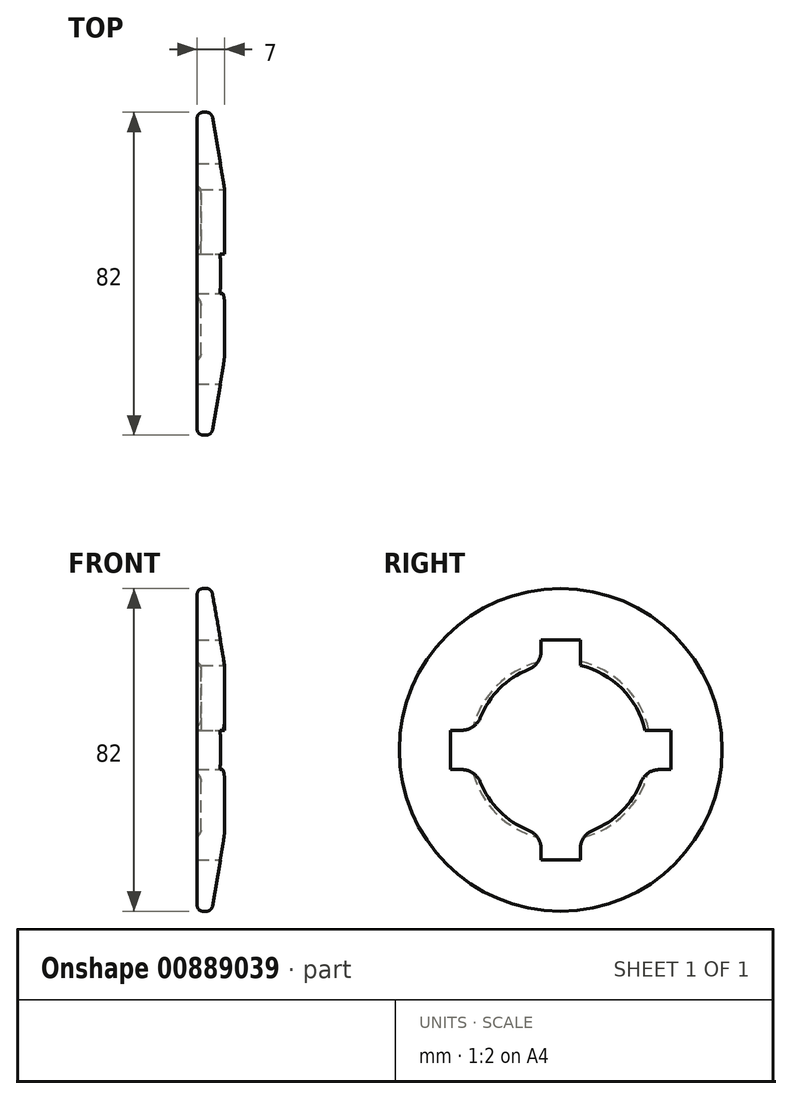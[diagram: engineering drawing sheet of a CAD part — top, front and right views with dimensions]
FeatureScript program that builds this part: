
annotation { "Feature Type Name" : "Feature", "Feature Type Description" : "" }
export const myFeature = defineFeature(function(context is Context, id is Id, definition is map)
    precondition{}
    {
        {
            var Q0;
            Q0=qCreatedBy(makeId("Front.planeOp"),FACE);
            var sketch = newSketch(context, id + "F0", { "sketchPlane" : qUnion([Q0])});
            skLineSegment(sketch, "E0", {"start": v(0, 0) * mm, "end": v(0, 22) * mm, "construction": true});
            skLineSegment(sketch, "E1", {"start": v(-3.35, 41) * mm, "end": v(0, 22) * mm});
            skLineSegment(sketch, "E2", {"start": v(-3.35, 41) * mm, "end": v(-7, 41) * mm});
            skLineSegment(sketch, "E3", {"start": v(-7, 41) * mm, "end": v(-7, 22) * mm});
            skLineSegment(sketch, "E4", {"start": v(-7, 22) * mm, "end": v(0, 22) * mm});
            skLineSegment(sketch, "E5", {"start": v(0, 0) * mm, "end": v(-22.75, 0) * mm, "construction": true});
            skSolve(sketch);
        }
        {
            var Q0;
            Q0=makeQuery(id+"F0.imprint","IMPRINT",FACE,{"disambiguationData":[TD([[makeQuery(id+"F0.imprint","IMPRINT",EDGE,{"derivedFrom":sQuery(id+"F0.wireOp",EDGE,"E1")}),-1.0]])]});
            var Q1;
            Q1=sQuery(id+"F0.wireOp",EDGE,"E5");
            revolve(context, id + "F1", {"surfaceOperationType" : NewSurfaceOperationType.NEW, "entities" : qUnion([Q0]), "axis" : qUnion([Q1]), "revolveType" : RevolveType.FULL});
        }
        {
            var Q0;
            Q0=qCreatedBy(makeId("Right.planeOp"),FACE);
            var sketch = newSketch(context, id + "F2", { "sketchPlane" : qUnion([Q0])});
            skLineSegment(sketch, "E6.top", {"start": v(5, 28) * mm, "end": v(0, 28) * mm});
            skLineSegment(sketch, "E6.left", {"start": v(5, 21.42) * mm, "end": v(5, 28) * mm});
            skArc(sketch, "E7.0", {"start": v(5, 21.42) * mm, "mid": v(0, 22) * mm, "end": v(-5, 21.42) * mm});
            skLineSegment(sketch, "E8.top", {"start": v(0, 28) * mm, "end": v(-5, 28) * mm});
            skLineSegment(sketch, "E8.right", {"start": v(-5, 21.42) * mm, "end": v(-5, 28) * mm});
            skLineSegment(sketch, "E9.1.0", {"start": v(-21.42, -5) * mm, "end": v(-28, -5) * mm});
            skArc(sketch, "E9.1.1", {"start": v(-21.42, 5) * mm, "mid": v(-22, 0) * mm, "end": v(-21.42, -5) * mm});
            skLineSegment(sketch, "E9.1.2", {"start": v(-21.42, 5) * mm, "end": v(-28, 5) * mm});
            skLineSegment(sketch, "E9.1.3", {"start": v(-28, 5) * mm, "end": v(-28, 0) * mm});
            skLineSegment(sketch, "E9.1.4", {"start": v(-28, 0) * mm, "end": v(-28, -5) * mm});
            skLineSegment(sketch, "E9.2.0", {"start": v(5, -21.42) * mm, "end": v(5, -28) * mm});
            skArc(sketch, "E9.2.1", {"start": v(-5, -21.42) * mm, "mid": v(0, -22) * mm, "end": v(5, -21.42) * mm});
            skLineSegment(sketch, "E9.2.2", {"start": v(-5, -21.42) * mm, "end": v(-5, -28) * mm});
            skLineSegment(sketch, "E9.2.3", {"start": v(-5, -28) * mm, "end": v(0, -28) * mm});
            skLineSegment(sketch, "E9.2.4", {"start": v(0, -28) * mm, "end": v(5, -28) * mm});
            skLineSegment(sketch, "E9.3.0", {"start": v(21.42, 5) * mm, "end": v(28, 5) * mm});
            skArc(sketch, "E9.3.1", {"start": v(21.42, -5) * mm, "mid": v(22, 0) * mm, "end": v(21.42, 5) * mm});
            skLineSegment(sketch, "E9.3.2", {"start": v(21.42, -5) * mm, "end": v(28, -5) * mm});
            skLineSegment(sketch, "E9.3.3", {"start": v(28, -5) * mm, "end": v(28, 0) * mm});
            skLineSegment(sketch, "E9.3.4", {"start": v(28, 0) * mm, "end": v(28, 5) * mm});
            skLineSegment(sketch, "E9.anchor1", {"start": v(0, 0) * mm, "end": v(-5, 21.42) * mm, "construction": true});
            skLineSegment(sketch, "E9.anchor2", {"start": v(0, 0) * mm, "end": v(21.42, 5) * mm, "construction": true});
            skSolve(sketch);
        }
        {
            var Q0;
            Q0 = qSketchRegion(id + "F2", true);
            extrude(context, id + "F3", {"entities" : qUnion([Q0]), "operationType" : NewBodyOperationType.REMOVE, "oppositeDirection" : true, "depth" : 25 * mm, "offsetDistance" : 25 * mm});
        }
        {
            var Q0;
            {var subQ0=sQuery(id+"F0.wireOp",EDGE,"E3");var subQ1=sQuery(id+"F0.wireOp",EDGE,"E4");Q0=makeQuery(id+"F3.boolean.opBoolean","SPLIT",EDGE,{"disambiguationData":[TD([makeQuery(id+"F3.opExtrude","SWEPT_FACE",FACE,{"disambiguationData":[OSD([sQuery(id+"F2.wireOp",EDGE,"E6.left")])]})])],"derivedFrom":makeQuery(id+"F1.opRevolve","SWEPT_EDGE",EDGE,{"disambiguationData":[OSD([subQ0,subQ1])]})});}
            var Q1;
            {var subQ0=sQuery(id+"F0.wireOp",EDGE,"E3");var subQ1=sQuery(id+"F0.wireOp",EDGE,"E4");Q1=makeQuery(id+"F3.boolean.opBoolean","SPLIT",EDGE,{"disambiguationData":[TD([makeQuery(id+"F3.opExtrude","SWEPT_FACE",FACE,{"disambiguationData":[OSD([sQuery(id+"F2.wireOp",EDGE,"E8.right")])]})])],"derivedFrom":makeQuery(id+"F1.opRevolve","SWEPT_EDGE",EDGE,{"disambiguationData":[OSD([subQ0,subQ1])]})});}
            var Q2;
            {var subQ0=sQuery(id+"F0.wireOp",EDGE,"E3");var subQ1=sQuery(id+"F0.wireOp",EDGE,"E4");Q2=makeQuery(id+"F3.boolean.opBoolean","SPLIT",EDGE,{"disambiguationData":[TD([makeQuery(id+"F3.opExtrude","SWEPT_FACE",FACE,{"disambiguationData":[OSD([sQuery(id+"F2.wireOp",EDGE,"E9.1.0")])]})])],"derivedFrom":makeQuery(id+"F1.opRevolve","SWEPT_EDGE",EDGE,{"disambiguationData":[OSD([subQ0,subQ1])]})});}
            var Q3;
            {var subQ0=sQuery(id+"F0.wireOp",EDGE,"E3");var subQ1=sQuery(id+"F0.wireOp",EDGE,"E4");Q3=makeQuery(id+"F3.boolean.opBoolean","SPLIT",EDGE,{"disambiguationData":[TD([makeQuery(id+"F3.opExtrude","SWEPT_FACE",FACE,{"disambiguationData":[OSD([sQuery(id+"F2.wireOp",EDGE,"E9.2.0")])]})])],"derivedFrom":makeQuery(id+"F1.opRevolve","SWEPT_EDGE",EDGE,{"disambiguationData":[OSD([subQ0,subQ1])]})});}
            chamfer(context, id + "F4", {"entities" : qUnion([Q0, Q1, Q2, Q3]), "width" : 1 * mm, "tangentPropagation" : true});
        }
        {
            var Q0;
            Q0=makeQuery(id+"F3.boolean.opBoolean","COPY",EDGE,{"derivedFrom":makeQuery(id+"F3.opExtrude","SWEPT_EDGE",EDGE,{"disambiguationData":[OSD([sQuery(id+"F2.wireOp",EDGE,"E9.2.1"),sQuery(id+"F2.wireOp",EDGE,"E9.2.2")])]})});
            var Q1;
            Q1=makeQuery(id+"F3.boolean.opBoolean","COPY",EDGE,{"derivedFrom":makeQuery(id+"F3.opExtrude","SWEPT_EDGE",EDGE,{"disambiguationData":[OSD([sQuery(id+"F2.wireOp",EDGE,"E9.2.0"),sQuery(id+"F2.wireOp",EDGE,"E9.2.1")])]})});
            var Q2;
            Q2=makeQuery(id+"F3.boolean.opBoolean","COPY",EDGE,{"derivedFrom":makeQuery(id+"F3.opExtrude","SWEPT_EDGE",EDGE,{"disambiguationData":[OSD([sQuery(id+"F2.wireOp",EDGE,"E9.3.1"),sQuery(id+"F2.wireOp",EDGE,"E9.3.2")])]})});
            var Q3;
            Q3=makeQuery(id+"F3.boolean.opBoolean","COPY",EDGE,{"derivedFrom":makeQuery(id+"F3.opExtrude","SWEPT_EDGE",EDGE,{"disambiguationData":[OSD([sQuery(id+"F2.wireOp",EDGE,"E9.3.0"),sQuery(id+"F2.wireOp",EDGE,"E9.3.1")])]})});
            var Q4;
            Q4=makeQuery(id+"F3.boolean.opBoolean","COPY",EDGE,{"derivedFrom":makeQuery(id+"F3.opExtrude","SWEPT_EDGE",EDGE,{"disambiguationData":[OSD([sQuery(id+"F2.wireOp",EDGE,"E6.left"),sQuery(id+"F2.wireOp",EDGE,"E7.0")])]})});
            var Q5;
            Q5=makeQuery(id+"F3.boolean.opBoolean","COPY",EDGE,{"derivedFrom":makeQuery(id+"F3.opExtrude","SWEPT_EDGE",EDGE,{"disambiguationData":[OSD([sQuery(id+"F2.wireOp",EDGE,"E7.0"),sQuery(id+"F2.wireOp",EDGE,"E8.right")])]})});
            var Q6;
            Q6=makeQuery(id+"F3.boolean.opBoolean","COPY",EDGE,{"derivedFrom":makeQuery(id+"F3.opExtrude","SWEPT_EDGE",EDGE,{"disambiguationData":[OSD([sQuery(id+"F2.wireOp",EDGE,"E9.1.1"),sQuery(id+"F2.wireOp",EDGE,"E9.1.2")])]})});
            var Q7;
            Q7=makeQuery(id+"F3.boolean.opBoolean","COPY",EDGE,{"derivedFrom":makeQuery(id+"F3.opExtrude","SWEPT_EDGE",EDGE,{"disambiguationData":[OSD([sQuery(id+"F2.wireOp",EDGE,"E9.1.0"),sQuery(id+"F2.wireOp",EDGE,"E9.1.1")])]})});
            fillet(context, id + "F5", {"entities" : qUnion([Q0, Q1, Q2, Q3, Q4, Q5, Q6, Q7]), "radius" : 5 * mm, "tangentPropagation" : true, "allowEdgeOverflow" : false});
        }
        {
            var Q0;
            Q0=makeQuery(id+"F1.opRevolve","SWEPT_EDGE",EDGE,{"disambiguationData":[OSD([sQuery(id+"F0.wireOp",EDGE,"E1"),sQuery(id+"F0.wireOp",EDGE,"E2")])]});
            var Q1;
            Q1=makeQuery(id+"F1.opRevolve","SWEPT_EDGE",EDGE,{"disambiguationData":[OSD([sQuery(id+"F0.wireOp",EDGE,"E2"),sQuery(id+"F0.wireOp",EDGE,"E3")])]});
            fillet(context, id + "F6", {"entities" : qUnion([Q0, Q1]), "radius" : 1.5 * mm, "tangentPropagation" : true, "allowEdgeOverflow" : false});
        }
    });
